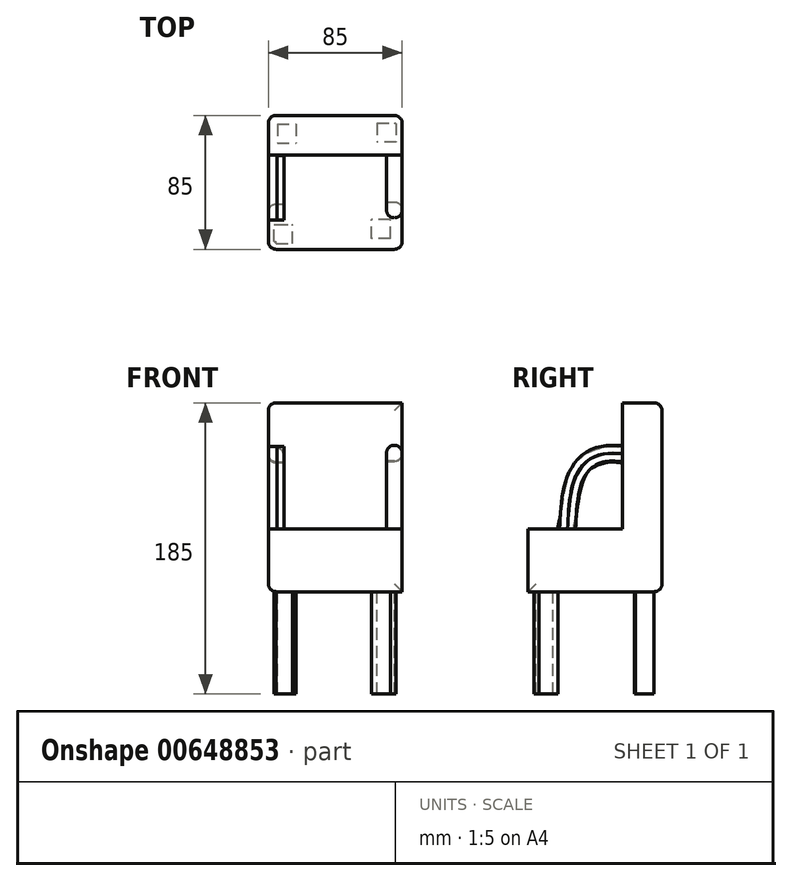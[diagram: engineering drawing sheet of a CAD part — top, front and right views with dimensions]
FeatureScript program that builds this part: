
annotation { "Feature Type Name" : "Feature", "Feature Type Description" : "" }
export const myFeature = defineFeature(function(context is Context, id is Id, definition is map)
    precondition{}
    {
        {
            var Q0;
            Q0=qCreatedBy(makeId("Right.planeOp"),FACE);
            var sketch = newSketch(context, id + "F0", { "sketchPlane" : qUnion([Q0])});
            skLineSegment(sketch, "E0.bottom", {"start": v(42.5, -60) * mm, "end": v(-42.5, -60) * mm});
            skLineSegment(sketch, "E0.top", {"start": v(42.5, 60) * mm, "end": v(-42.5, 60) * mm});
            skLineSegment(sketch, "E0.left", {"start": v(42.5, -60) * mm, "end": v(42.5, 60) * mm});
            skLineSegment(sketch, "E0.right", {"start": v(-42.5, -60) * mm, "end": v(-42.5, 60) * mm});
            skPoint(sketch, "E0.middle", {"position": v(0, 0) * mm});
            skSolve(sketch);
        }
        {
            var Q0;
            Q0 = qSketchRegion(id + "F0", true);
            extrude(context, id + "F1", {"entities" : qUnion([Q0]), "depth" : 85 * mm, "offsetDistance" : 25 * mm});
        }
        {
            var Q0;
            Q0=makeQuery(id+"F1.opExtrude","CAP_FACE",FACE,{"disambiguationData":[OSD([sQuery(id+"F0.wireOp",EDGE,"E0.bottom"),sQuery(id+"F0.wireOp",EDGE,"E0.top"),sQuery(id+"F0.wireOp",EDGE,"E0.left"),sQuery(id+"F0.wireOp",EDGE,"E0.right")])],"isStart":false});
            var sketch = newSketch(context, id + "F2", { "sketchPlane" : qUnion([Q0])});
            skLineSegment(sketch, "E1", {"start": v(-42.5, 60) * mm, "end": v(17.5, 60) * mm});
            skLineSegment(sketch, "E2", {"start": v(17.5, 60) * mm, "end": v(17.5, -20) * mm});
            skLineSegment(sketch, "E3", {"start": v(17.5, -20) * mm, "end": v(-42.5, -20) * mm});
            skLineSegment(sketch, "E4", {"start": v(-42.5, 60) * mm, "end": v(-42.5, -20) * mm});
            skSolve(sketch);
        }
        {
            var Q0;
            Q0=makeQuery(id+"F1.opExtrude","CAP_FACE",FACE,{"disambiguationData":[OSD([sQuery(id+"F0.wireOp",EDGE,"E0.bottom"),sQuery(id+"F0.wireOp",EDGE,"E0.top"),sQuery(id+"F0.wireOp",EDGE,"E0.left"),sQuery(id+"F0.wireOp",EDGE,"E0.right")])],"isStart":true});
            var sketch = newSketch(context, id + "F3", { "sketchPlane" : qUnion([Q0])});
            skLineSegment(sketch, "E5", {"start": v(42.5, 60) * mm, "end": v(-17.5, 60) * mm});
            skLineSegment(sketch, "E6", {"start": v(-17.5, 60) * mm, "end": v(-17.5, -20) * mm});
            skLineSegment(sketch, "E7", {"start": v(-17.5, -20) * mm, "end": v(42.5, -20) * mm});
            skLineSegment(sketch, "E8", {"start": v(42.5, 60) * mm, "end": v(42.5, -20) * mm});
            skSolve(sketch);
        }
        {
            var Q0;
            Q0=makeQuery(id+"F2.imprint","IMPRINT",FACE,{"disambiguationData":[TD([[makeQuery(id+"F2.imprint","IMPRINT",EDGE,{"derivedFrom":sQuery(id+"F2.wireOp",EDGE,"E1")}),1.0]])]});
            extrude(context, id + "F4", {"entities" : qUnion([Q0]), "operationType" : NewBodyOperationType.REMOVE, "oppositeDirection" : true, "depth" : 85 * mm, "offsetDistance" : 25 * mm});
        }
        {
            var Q0;
            Q0=makeQuery(id+"F4.boolean.opBoolean","COPY",FACE,{"derivedFrom":makeQuery(id+"F4.opExtrude","SWEPT_FACE",FACE,{"disambiguationData":[OSD([sQuery(id+"F2.wireOp",EDGE,"E2")])]})});
            var sketch = newSketch(context, id + "F5", { "sketchPlane" : qUnion([Q0])});
            skLineSegment(sketch, "E9.bottom", {"start": v(0, 32.62) * mm, "end": v(10, 32.62) * mm});
            skLineSegment(sketch, "E9.top", {"start": v(0, 22.62) * mm, "end": v(10, 22.62) * mm});
            skLineSegment(sketch, "E9.left", {"start": v(0, 32.62) * mm, "end": v(0, 22.62) * mm});
            skLineSegment(sketch, "E9.right", {"start": v(10, 32.62) * mm, "end": v(10, 22.62) * mm});
            skLineSegment(sketch, "E10.bottom", {"start": v(85, 22.62) * mm, "end": v(75, 22.62) * mm});
            skLineSegment(sketch, "E10.top", {"start": v(85, 32.62) * mm, "end": v(75, 32.62) * mm});
            skLineSegment(sketch, "E10.left", {"start": v(85, 22.62) * mm, "end": v(85, 32.62) * mm});
            skLineSegment(sketch, "E10.right", {"start": v(75, 22.62) * mm, "end": v(75, 32.62) * mm});
            skSolve(sketch);
        }
        {
            var Q0;
            Q0=makeQuery(id+"F4.boolean.opBoolean","COPY",FACE,{"derivedFrom":makeQuery(id+"F4.opExtrude","SWEPT_FACE",FACE,{"disambiguationData":[OSD([sQuery(id+"F2.wireOp",EDGE,"E3")])]})});
            var sketch = newSketch(context, id + "F6", { "sketchPlane" : qUnion([Q0])});
            skLineSegment(sketch, "E11.bottom", {"start": v(0, -12.5) * mm, "end": v(10, -12.5) * mm});
            skLineSegment(sketch, "E11.top", {"start": v(0, -22.5) * mm, "end": v(10, -22.5) * mm});
            skLineSegment(sketch, "E11.left", {"start": v(0, -12.5) * mm, "end": v(0, -22.5) * mm});
            skLineSegment(sketch, "E11.right", {"start": v(10, -12.5) * mm, "end": v(10, -22.5) * mm});
            skLineSegment(sketch, "E12.bottom", {"start": v(85, -22.5) * mm, "end": v(75, -22.5) * mm});
            skLineSegment(sketch, "E12.top", {"start": v(85, -12.5) * mm, "end": v(75, -12.5) * mm});
            skLineSegment(sketch, "E12.left", {"start": v(85, -22.5) * mm, "end": v(85, -12.5) * mm});
            skLineSegment(sketch, "E12.right", {"start": v(75, -22.5) * mm, "end": v(75, -12.5) * mm});
            skSolve(sketch);
        }
        {
            var Q0;
            {var subQ2=sQuery(id+"F3.wireOp",EDGE,"E6");Q0=makeQuery(id+"F3.imprint","IMPRINT",FACE,{"disambiguationData":[TD([[makeQuery(id+"F3.imprint","IMPRINT",EDGE,{"derivedFrom":subQ2}),-1.0]])]});}
            cPlane(context, id + "F7", {"entities" : qUnion([Q0]), "cplaneType" : CPlaneType.OFFSET, "offset" : 5 * mm, "oppositeDirection" : true, "width" : 150 * mm, "height" : 150 * mm});
        }
        {
            var Q0;
            Q0=makeQuery(id+"F1.opExtrude","CAP_FACE",FACE,{"disambiguationData":[OSD([sQuery(id+"F0.wireOp",EDGE,"E0.bottom"),sQuery(id+"F0.wireOp",EDGE,"E0.top"),sQuery(id+"F0.wireOp",EDGE,"E0.left"),sQuery(id+"F0.wireOp",EDGE,"E0.right")])],"isStart":false});
            cPlane(context, id + "F8", {"entities" : qUnion([Q0]), "cplaneType" : CPlaneType.OFFSET, "offset" : 5 * mm, "oppositeDirection" : true, "width" : 150 * mm, "height" : 150 * mm});
        }
        {
            var Q0;
            Q0=qCreatedBy(id+"F8.planeOp",FACE);
            var sketch = newSketch(context, id + "F9", { "sketchPlane" : qUnion([Q0])});
            skFitSpline(sketch, "E13", {"points": [v(18.46, 27.05) * mm, v(8.44, 27.33) * mm, v(-3.3, 23.61) * mm, v(-11.3, 13.88) * mm, v(-14.74, 3.3) * mm, v(-16.46, -11.6) * mm, v(-17.03, -22.75) * mm], "startDerivative": vector(-63.68, 5.69) * mm, "endDerivative": vector(-2.65, -65.75) * mm});
            skSolve(sketch);
        }
        {
            var Q0;
            Q0=makeQuery(id+"F5.imprint","IMPRINT",FACE,{"disambiguationData":[TD([[makeQuery(id+"F5.imprint","IMPRINT",EDGE,{"derivedFrom":sQuery(id+"F5.wireOp",EDGE,"E10.bottom")}),-1.0]])]});
            var Q1;
            Q1=makeQuery(id+"F6.imprint","IMPRINT",FACE,{"disambiguationData":[TD([[makeQuery(id+"F6.imprint","IMPRINT",EDGE,{"derivedFrom":sQuery(id+"F6.wireOp",EDGE,"E12.bottom")}),-1.0]])]});
            var Q2;
            Q2=sQuery(id+"F9.wireOp",EDGE,"E13");
            sweep(context, id + "F10", {"operationType" : NewBodyOperationType.ADD, "profiles" : qUnion([Q0, Q1]), "path" : qUnion([Q2])});
        }
        {
            var Q0;
            Q0=makeQuery(id+"F4.boolean.opBoolean","COPY",FACE,{"derivedFrom":makeQuery(id+"F4.opExtrude","SWEPT_FACE",FACE,{"disambiguationData":[OSD([sQuery(id+"F2.wireOp",EDGE,"E2")])]})});
            var sketch = newSketch(context, id + "F11", { "sketchPlane" : qUnion([Q0])});
            skLineSegment(sketch, "E14.bottom", {"start": v(9.6, 21.7) * mm, "end": v(-0.4, 21.7) * mm});
            skLineSegment(sketch, "E14.top", {"start": v(9.6, 31.7) * mm, "end": v(-0.4, 31.7) * mm});
            skLineSegment(sketch, "E14.left", {"start": v(9.6, 21.7) * mm, "end": v(9.6, 31.7) * mm});
            skLineSegment(sketch, "E14.right", {"start": v(-0.4, 21.7) * mm, "end": v(-0.4, 31.7) * mm});
            skPoint(sketch, "E14.middle", {"position": v(4.6, 26.7) * mm});
            skSolve(sketch);
        }
        {
            var Q0;
            Q0=makeQuery(id+"F4.boolean.opBoolean","COPY",FACE,{"derivedFrom":makeQuery(id+"F4.opExtrude","SWEPT_FACE",FACE,{"disambiguationData":[OSD([sQuery(id+"F2.wireOp",EDGE,"E3")])]})});
            var sketch = newSketch(context, id + "F12", { "sketchPlane" : qUnion([Q0])});
            skLineSegment(sketch, "E15.bottom", {"start": v(9.91, -23.82) * mm, "end": v(-0.09, -23.82) * mm});
            skLineSegment(sketch, "E15.top", {"start": v(9.91, -13.82) * mm, "end": v(-0.09, -13.82) * mm});
            skLineSegment(sketch, "E15.left", {"start": v(9.91, -23.82) * mm, "end": v(9.91, -13.82) * mm});
            skLineSegment(sketch, "E15.right", {"start": v(-0.09, -23.82) * mm, "end": v(-0.09, -13.82) * mm});
            skPoint(sketch, "E15.middle", {"position": v(4.91, -18.82) * mm});
            skSolve(sketch);
        }
        {
            var Q0;
            Q0=qCreatedBy(id+"F7.planeOp",FACE);
            var sketch = newSketch(context, id + "F13", { "sketchPlane" : qUnion([Q0])});
            skFitSpline(sketch, "E16", {"points": [v(-17.32, 26.76) * mm, v(-9.59, 27.33) * mm, v(0, 25.04) * mm, v(8.16, 19.6) * mm, v(13.02, 9.87) * mm, v(15.31, 0) * mm, v(16.74, -9.59) * mm, v(19.03, -20.75) * mm], "startDerivative": vector(59.3, 8.7) * mm, "endDerivative": vector(16.5, -74.2) * mm});
            skSolve(sketch);
        }
        {
            var Q0;
            {var subQ0=sQuery(id+"F11.wireOp",EDGE,"E14.left");Q0=makeQuery(id+"F11.imprint","IMPRINT",FACE,{"disambiguationData":[TD([[makeQuery(id+"F11.imprint","IMPRINT",EDGE,{"derivedFrom":subQ0}),1.0]])]});}
            var Q1;
            {var subQ0=sQuery(id+"F12.wireOp",EDGE,"E15.left");Q1=makeQuery(id+"F12.imprint","IMPRINT",FACE,{"disambiguationData":[TD([[makeQuery(id+"F12.imprint","IMPRINT",EDGE,{"derivedFrom":subQ0}),1.0]])]});}
            var Q2;
            Q2=sQuery(id+"F13.wireOp",EDGE,"E16");
            sweep(context, id + "F14", {"operationType" : NewBodyOperationType.ADD, "profiles" : qUnion([Q0, Q1]), "path" : qUnion([Q2])});
        }
        {
            var Q0;
            Q0=makeQuery(id+"F1.opExtrude","SWEPT_FACE",FACE,{"disambiguationData":[OSD([sQuery(id+"F0.wireOp",EDGE,"E0.bottom")])]});
            var sketch = newSketch(context, id + "F15", { "sketchPlane" : qUnion([Q0])});
            skLineSegment(sketch, "E17.bottom", {"start": v(0, 42.5) * mm, "end": v(5, 42.5) * mm});
            skLineSegment(sketch, "E17.top", {"start": v(0, 37.5) * mm, "end": v(5, 37.5) * mm});
            skLineSegment(sketch, "E17.left", {"start": v(0, 42.5) * mm, "end": v(0, 37.5) * mm});
            skLineSegment(sketch, "E17.right", {"start": v(5, 42.5) * mm, "end": v(5, 37.5) * mm});
            skLineSegment(sketch, "E18.bottom", {"start": v(80, 42.5) * mm, "end": v(85, 42.5) * mm});
            skLineSegment(sketch, "E18.top", {"start": v(80, 37.5) * mm, "end": v(85, 37.5) * mm});
            skLineSegment(sketch, "E18.left", {"start": v(80, 42.5) * mm, "end": v(80, 37.5) * mm});
            skLineSegment(sketch, "E18.right", {"start": v(85, 42.5) * mm, "end": v(85, 37.5) * mm});
            skLineSegment(sketch, "E19.bottom", {"start": v(0, -37.5) * mm, "end": v(5, -37.5) * mm});
            skLineSegment(sketch, "E19.top", {"start": v(0, -42.5) * mm, "end": v(5, -42.5) * mm});
            skLineSegment(sketch, "E19.left", {"start": v(0, -37.5) * mm, "end": v(0, -42.5) * mm});
            skLineSegment(sketch, "E19.right", {"start": v(5, -37.5) * mm, "end": v(5, -42.5) * mm});
            skLineSegment(sketch, "E20.bottom", {"start": v(85, -42.5) * mm, "end": v(80, -42.5) * mm});
            skLineSegment(sketch, "E20.top", {"start": v(85, -37.5) * mm, "end": v(80, -37.5) * mm});
            skLineSegment(sketch, "E20.left", {"start": v(85, -42.5) * mm, "end": v(85, -37.5) * mm});
            skLineSegment(sketch, "E20.right", {"start": v(80, -42.5) * mm, "end": v(80, -37.5) * mm});
            skSolve(sketch);
        }
        {
            var Q0;
            {var subQ4=sQuery(id+"F15.wireOp",EDGE,"E17.top");Q0=makeQuery(id+"F15.imprint","IMPRINT",FACE,{"disambiguationData":[TD([[makeQuery(id+"F15.imprint","IMPRINT",EDGE,{"derivedFrom":subQ4}),-1.0]])]});}
            var sketch = newSketch(context, id + "F16", { "sketchPlane" : qUnion([Q0])});
            skLineSegment(sketch, "E21.bottom", {"start": v(3.45, 38.76) * mm, "end": v(15.45, 38.76) * mm});
            skLineSegment(sketch, "E21.top", {"start": v(3.45, 26.76) * mm, "end": v(15.45, 26.76) * mm});
            skLineSegment(sketch, "E21.left", {"start": v(3.45, 38.76) * mm, "end": v(3.45, 26.76) * mm});
            skLineSegment(sketch, "E21.right", {"start": v(15.45, 38.76) * mm, "end": v(15.45, 26.76) * mm});
            skSolve(sketch);
        }
        {
            var Q0;
            {var subQ2=sQuery(id+"F16.wireOp",EDGE,"E21.top");Q0=makeQuery(id+"F16.imprint","IMPRINT",FACE,{"disambiguationData":[TD([[makeQuery(id+"F16.imprint","IMPRINT",EDGE,{"derivedFrom":subQ2}),1.0]])]});}
            extrude(context, id + "F17", {"entities" : qUnion([Q0]), "operationType" : NewBodyOperationType.ADD, "depth" : 65 * mm, "offsetDistance" : 25 * mm});
        }
        {
            var Q0;
            {var subQ4=sQuery(id+"F15.wireOp",EDGE,"E17.top");Q0=makeQuery(id+"F15.imprint","IMPRINT",FACE,{"disambiguationData":[TD([[makeQuery(id+"F15.imprint","IMPRINT",EDGE,{"derivedFrom":subQ4}),-1.0]])]});}
            var sketch = newSketch(context, id + "F18", { "sketchPlane" : qUnion([Q0])});
            skLineSegment(sketch, "E22.bottom", {"start": v(77.55, 35.69) * mm, "end": v(65.55, 35.69) * mm});
            skLineSegment(sketch, "E22.top", {"start": v(77.55, 23.69) * mm, "end": v(65.55, 23.69) * mm});
            skLineSegment(sketch, "E22.left", {"start": v(77.55, 35.69) * mm, "end": v(77.55, 23.69) * mm});
            skLineSegment(sketch, "E22.right", {"start": v(65.55, 35.69) * mm, "end": v(65.55, 23.69) * mm});
            skLineSegment(sketch, "E23.bottom", {"start": v(79.52, -36.16) * mm, "end": v(67.52, -36.16) * mm});
            skLineSegment(sketch, "E23.top", {"start": v(79.52, -24.16) * mm, "end": v(67.52, -24.16) * mm});
            skLineSegment(sketch, "E23.left", {"start": v(79.52, -36.16) * mm, "end": v(79.52, -24.16) * mm});
            skLineSegment(sketch, "E23.right", {"start": v(67.52, -36.16) * mm, "end": v(67.52, -24.16) * mm});
            skLineSegment(sketch, "E24.bottom", {"start": v(5.61, -36.6) * mm, "end": v(17.61, -36.6) * mm});
            skLineSegment(sketch, "E24.top", {"start": v(5.61, -24.6) * mm, "end": v(17.61, -24.6) * mm});
            skLineSegment(sketch, "E24.left", {"start": v(5.61, -36.6) * mm, "end": v(5.61, -24.6) * mm});
            skLineSegment(sketch, "E24.right", {"start": v(17.61, -36.6) * mm, "end": v(17.61, -24.6) * mm});
            skSolve(sketch);
        }
        {
            var Q0;
            Q0=makeQuery(id+"F18.imprint","IMPRINT",FACE,{"disambiguationData":[TD([[makeQuery(id+"F18.imprint","IMPRINT",EDGE,{"derivedFrom":sQuery(id+"F18.wireOp",EDGE,"E22.bottom")}),1.0]])]});
            extrude(context, id + "F19", {"entities" : qUnion([Q0]), "operationType" : NewBodyOperationType.ADD, "depth" : 65 * mm, "offsetDistance" : 25 * mm});
        }
        {
            var Q0;
            {var subQ4=sQuery(id+"F15.wireOp",EDGE,"E17.top");Q0=makeQuery(id+"F15.imprint","IMPRINT",FACE,{"disambiguationData":[TD([[makeQuery(id+"F15.imprint","IMPRINT",EDGE,{"derivedFrom":subQ4}),-1.0]])]});}
            var sketch = newSketch(context, id + "F20", { "sketchPlane" : qUnion([Q0])});
            skLineSegment(sketch, "E25.bottom", {"start": v(5.7, -36.93) * mm, "end": v(17.7, -36.93) * mm});
            skLineSegment(sketch, "E25.top", {"start": v(5.7, -24.93) * mm, "end": v(17.7, -24.93) * mm});
            skLineSegment(sketch, "E25.left", {"start": v(5.7, -36.93) * mm, "end": v(5.7, -24.93) * mm});
            skLineSegment(sketch, "E25.right", {"start": v(17.7, -36.93) * mm, "end": v(17.7, -24.93) * mm});
            skSolve(sketch);
        }
        {
            var Q0;
            Q0=makeQuery(id+"F20.imprint","IMPRINT",FACE,{"disambiguationData":[TD([[makeQuery(id+"F20.imprint","IMPRINT",EDGE,{"derivedFrom":sQuery(id+"F20.wireOp",EDGE,"E25.bottom")}),1.0]])]});
            extrude(context, id + "F21", {"entities" : qUnion([Q0]), "operationType" : NewBodyOperationType.ADD, "depth" : 65 * mm, "offsetDistance" : 25 * mm});
        }
        {
            var Q0;
            {var subQ4=sQuery(id+"F15.wireOp",EDGE,"E17.top");Q0=makeQuery(id+"F15.imprint","IMPRINT",FACE,{"disambiguationData":[TD([[makeQuery(id+"F15.imprint","IMPRINT",EDGE,{"derivedFrom":subQ4}),-1.0]])]});}
            var sketch = newSketch(context, id + "F22", { "sketchPlane" : qUnion([Q0])});
            skLineSegment(sketch, "E26.bottom", {"start": v(81.13, -37.52) * mm, "end": v(69.13, -37.52) * mm});
            skLineSegment(sketch, "E26.top", {"start": v(81.13, -25.52) * mm, "end": v(69.13, -25.52) * mm});
            skLineSegment(sketch, "E26.left", {"start": v(81.13, -37.52) * mm, "end": v(81.13, -25.52) * mm});
            skLineSegment(sketch, "E26.right", {"start": v(69.13, -37.52) * mm, "end": v(69.13, -25.52) * mm});
            skSolve(sketch);
        }
        {
            var Q0;
            {var subQ2=sQuery(id+"F22.wireOp",EDGE,"E26.top");Q0=makeQuery(id+"F22.imprint","IMPRINT",FACE,{"disambiguationData":[TD([[makeQuery(id+"F22.imprint","IMPRINT",EDGE,{"derivedFrom":subQ2}),1.0]])]});}
            extrude(context, id + "F23", {"entities" : qUnion([Q0]), "operationType" : NewBodyOperationType.ADD, "depth" : 65 * mm, "offsetDistance" : 25 * mm});
        }
        {
            var Q0;
            Q0=makeQuery(id+"F4.boolean.opBoolean","COPY",EDGE,{"derivedFrom":makeQuery(id+"F4.opExtrude","SWEPT_EDGE",EDGE,{"disambiguationData":[OSD([sQuery(id+"F0.wireOp",EDGE,"E0.right"),sQuery(id+"F2.wireOp",EDGE,"E3"),sQuery(id+"F2.wireOp",EDGE,"E4")])]})});
            var Q1;
            Q1=makeQuery(id+"F1.opExtrude","CAP_EDGE",EDGE,{"disambiguationData":[OSD([sQuery(id+"F0.wireOp",EDGE,"E0.right")])],"isStart":false});
            var Q2;
            Q2=makeQuery(id+"F1.opExtrude","CAP_EDGE",EDGE,{"disambiguationData":[OSD([sQuery(id+"F0.wireOp",EDGE,"E0.right")])],"isStart":true});
            var Q3;
            Q3=makeQuery(id+"F1.opExtrude","CAP_EDGE",EDGE,{"disambiguationData":[OSD([sQuery(id+"F0.wireOp",EDGE,"E0.bottom")])],"isStart":true});
            var Q4;
            Q4=makeQuery(id+"F1.opExtrude","CAP_EDGE",EDGE,{"disambiguationData":[OSD([sQuery(id+"F0.wireOp",EDGE,"E0.left")])],"isStart":true});
            var Q5;
            {var subQ1=sQuery(id+"F2.wireOp",EDGE,"E3");var subQ2=sQuery(id+"F2.wireOp",EDGE,"E2");Q5=makeQuery(id+"F14.boolean.opBoolean","SPLIT",EDGE,{"disambiguationData":[TD([makeQuery(id+"F4.boolean.opBoolean","COPY",FACE,{"derivedFrom":makeQuery(id+"F4.opExtrude","SWEPT_FACE",FACE,{"disambiguationData":[OSD([subQ1])]})})])],"derivedFrom":makeQuery(id+"F4.boolean.opBoolean","COPY",EDGE,{"derivedFrom":makeQuery(id+"F4.opExtrude","CAP_EDGE",EDGE,{"disambiguationData":[OSD([subQ2])],"isStart":false})})});}
            var Q6;
            Q6=makeQuery(id+"F14.opSweep","SWEPT_EDGE",EDGE,{"disambiguationData":[OSD([sQuery(id+"F2.wireOp",EDGE,"E2"),sQuery(id+"F11.wireOp",EDGE,"E14.bottom"),sQuery(id+"F13.wireOp",EDGE,"E16")])]});
            var Q7;
            Q7=makeQuery(id+"F1.opExtrude","SWEPT_EDGE",EDGE,{"disambiguationData":[OSD([sQuery(id+"F0.wireOp",EDGE,"E0.top"),sQuery(id+"F0.wireOp",EDGE,"E0.left")])]});
            var Q8;
            Q8=makeQuery(id+"F4.boolean.opBoolean","COPY",EDGE,{"derivedFrom":makeQuery(id+"F4.opExtrude","SWEPT_EDGE",EDGE,{"disambiguationData":[OSD([sQuery(id+"F0.wireOp",EDGE,"E0.top"),sQuery(id+"F2.wireOp",EDGE,"E1"),sQuery(id+"F2.wireOp",EDGE,"E2")])]})});
            var Q9;
            Q9=makeQuery(id+"F1.opExtrude","CAP_EDGE",EDGE,{"disambiguationData":[OSD([sQuery(id+"F0.wireOp",EDGE,"E0.top")])],"isStart":true});
            var Q10;
            Q10=makeQuery(id+"F10.opSweep","SWEPT_EDGE",EDGE,{"disambiguationData":[OSD([sQuery(id+"F2.wireOp",EDGE,"E2"),sQuery(id+"F5.wireOp",EDGE,"E10.bottom"),sQuery(id+"F5.wireOp",EDGE,"E10.left"),sQuery(id+"F9.wireOp",EDGE,"E13")])]});
            var Q11;
            Q11=makeQuery(id+"F10.opSweep","SWEPT_EDGE",EDGE,{"disambiguationData":[OSD([sQuery(id+"F6.wireOp",EDGE,"E12.bottom"),sQuery(id+"F6.wireOp",EDGE,"E12.right"),sQuery(id+"F9.wireOp",EDGE,"E13")])]});
            var Q12;
            Q12=makeQuery(id+"F10.opSweep","SWEPT_EDGE",EDGE,{"disambiguationData":[OSD([sQuery(id+"F2.wireOp",EDGE,"E3"),sQuery(id+"F6.wireOp",EDGE,"E12.bottom"),sQuery(id+"F6.wireOp",EDGE,"E12.left"),sQuery(id+"F9.wireOp",EDGE,"E13")])]});
            var Q13;
            Q13=makeQuery(id+"F14.opSweep","SWEPT_EDGE",EDGE,{"disambiguationData":[OSD([sQuery(id+"F11.wireOp",EDGE,"E14.top"),sQuery(id+"F11.wireOp",EDGE,"E14.left"),sQuery(id+"F13.wireOp",EDGE,"E16")])]});
            var Q14;
            {var subQ1=sQuery(id+"F2.wireOp",EDGE,"E3");Q14=makeQuery(id+"F10.boolean.opBoolean","SPLIT",EDGE,{"disambiguationData":[TD([makeQuery(id+"F4.boolean.opBoolean","COPY",FACE,{"derivedFrom":makeQuery(id+"F4.opExtrude","SWEPT_FACE",FACE,{"disambiguationData":[OSD([sQuery(id+"F2.wireOp",EDGE,"E2")])]})})])],"derivedFrom":makeQuery(id+"F4.boolean.opBoolean","COPY",EDGE,{"derivedFrom":makeQuery(id+"F4.opExtrude","CAP_EDGE",EDGE,{"disambiguationData":[OSD([subQ1])],"isStart":true})})});}
            var Q15;
            {var subQ1=sQuery(id+"F2.wireOp",EDGE,"E2");Q15=makeQuery(id+"F10.boolean.opBoolean","SPLIT",EDGE,{"disambiguationData":[TD([makeQuery(id+"F4.boolean.opBoolean","COPY",FACE,{"derivedFrom":makeQuery(id+"F4.opExtrude","SWEPT_FACE",FACE,{"disambiguationData":[OSD([sQuery(id+"F2.wireOp",EDGE,"E3")])]})})])],"derivedFrom":makeQuery(id+"F4.boolean.opBoolean","COPY",EDGE,{"derivedFrom":makeQuery(id+"F4.opExtrude","CAP_EDGE",EDGE,{"disambiguationData":[OSD([subQ1])],"isStart":true})})});}
            var Q16;
            {var subQ0=sQuery(id+"F2.wireOp",EDGE,"E2");var subQ1=sQuery(id+"F0.wireOp",EDGE,"E0.top");Q16=makeQuery(id+"F10.boolean.opBoolean","SPLIT",EDGE,{"disambiguationData":[TD([makeQuery(id+"F1.opExtrude","SWEPT_FACE",FACE,{"disambiguationData":[OSD([subQ1])]})])],"derivedFrom":makeQuery(id+"F4.boolean.opBoolean","COPY",EDGE,{"derivedFrom":makeQuery(id+"F4.opExtrude","CAP_EDGE",EDGE,{"disambiguationData":[OSD([subQ0])],"isStart":true})})});}
            var Q17;
            Q17=makeQuery(id+"F1.opExtrude","CAP_EDGE",EDGE,{"disambiguationData":[OSD([sQuery(id+"F0.wireOp",EDGE,"E0.left")])],"isStart":false});
            var Q18;
            Q18=makeQuery(id+"F1.opExtrude","SWEPT_EDGE",EDGE,{"disambiguationData":[OSD([sQuery(id+"F0.wireOp",EDGE,"E0.bottom"),sQuery(id+"F0.wireOp",EDGE,"E0.left")])]});
            fillet(context, id + "F24", {"entities" : qUnion([Q0, Q1, Q2, Q3, Q4, Q5, Q6, Q7, Q8, Q9, Q10, Q11, Q12, Q13, Q14, Q15, Q16, Q17, Q18]), "radius" : 5 * mm, "tangentPropagation" : true, "allowEdgeOverflow" : false});
        }
    });
